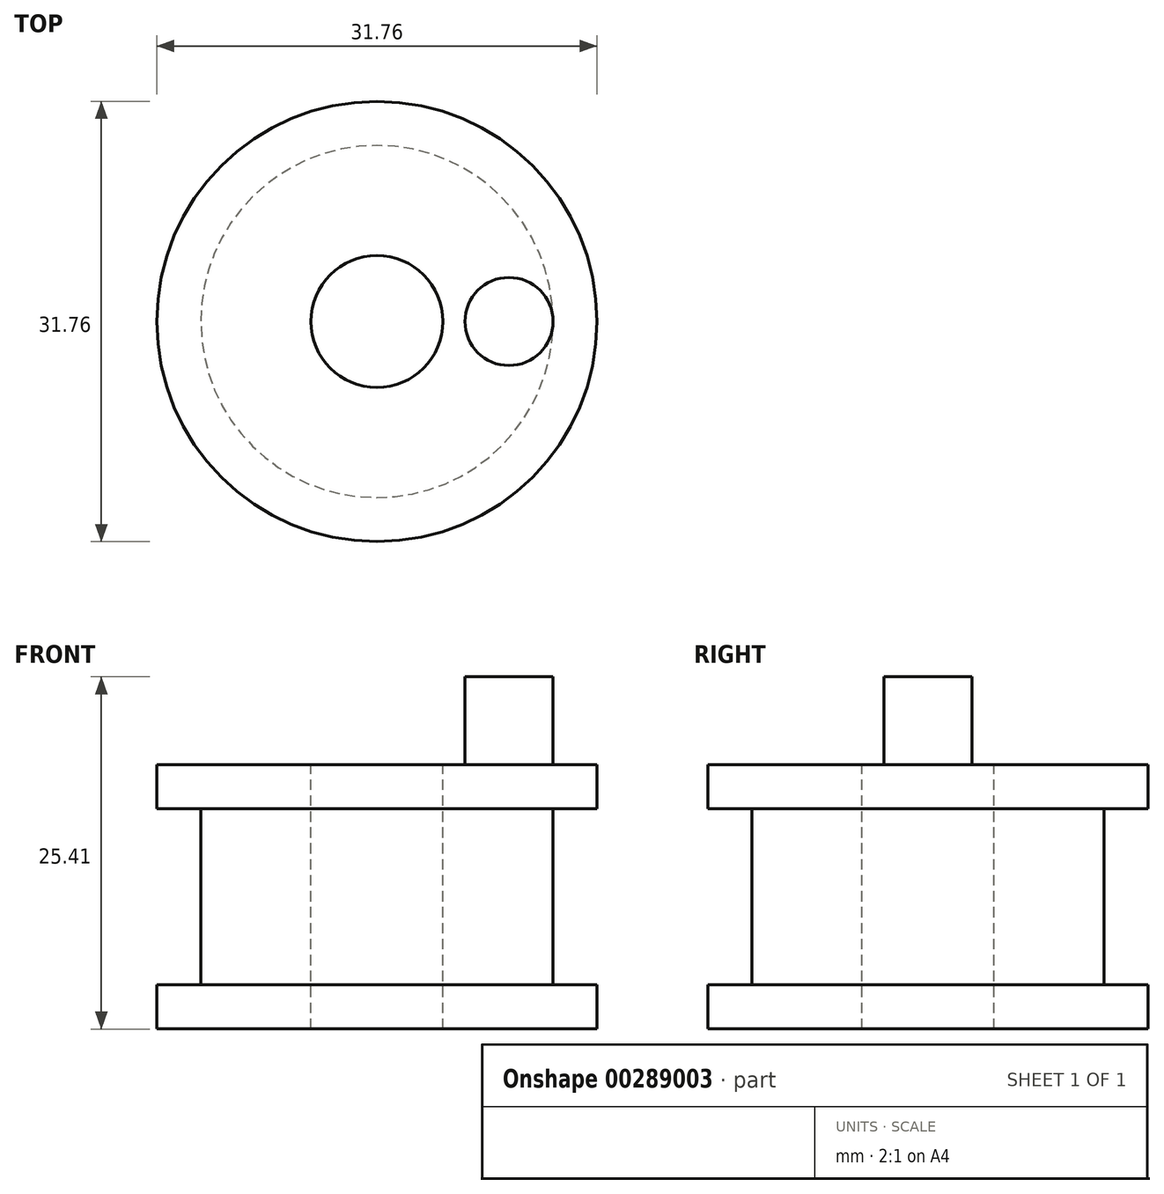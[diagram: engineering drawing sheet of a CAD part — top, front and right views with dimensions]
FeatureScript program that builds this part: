
annotation { "Feature Type Name" : "Feature", "Feature Type Description" : "" }
export const myFeature = defineFeature(function(context is Context, id is Id, definition is map)
    precondition{}
    {
        {
            var Q0;
            Q0=qCreatedBy(makeId("Front.planeOp"),FACE);
            var sketch = newSketch(context, id + "F0", { "sketchPlane" : qUnion([Q0])});
            skLineSegment(sketch, "E0.bottom", {"start": v(-12.7, 6.35) * mm, "end": v(12.7, 6.35) * mm});
            skLineSegment(sketch, "E0.top", {"start": v(-12.7, -6.35) * mm, "end": v(12.7, -6.35) * mm});
            skLineSegment(sketch, "E0.left", {"start": v(-12.7, 6.35) * mm, "end": v(-12.7, -6.35) * mm});
            skLineSegment(sketch, "E0.right", {"start": v(12.7, 6.35) * mm, "end": v(12.7, -6.35) * mm});
            skPoint(sketch, "E0.middle", {"position": v(0, 0) * mm});
            skLineSegment(sketch, "E1", {"start": v(-12.7, 6.35) * mm, "end": v(-15.88, 6.35) * mm});
            skLineSegment(sketch, "E2", {"start": v(-15.88, 6.35) * mm, "end": v(-15.88, 9.53) * mm});
            skLineSegment(sketch, "E3", {"start": v(12.7, 6.35) * mm, "end": v(15.88, 6.35) * mm});
            skLineSegment(sketch, "E4.bottom", {"start": v(-15.88, 6.35) * mm, "end": v(15.88, 6.35) * mm});
            skLineSegment(sketch, "E4.top", {"start": v(-15.88, 9.53) * mm, "end": v(15.88, 9.53) * mm});
            skLineSegment(sketch, "E4.right", {"start": v(15.88, 6.35) * mm, "end": v(15.88, 9.53) * mm});
            skLineSegment(sketch, "E5.MirrorCS", {"start": v(-15.88, -9.53) * mm, "end": v(15.88, -9.53) * mm});
            skLineSegment(sketch, "E6.MirrorCS", {"start": v(-15.88, -6.35) * mm, "end": v(15.88, -6.35) * mm});
            skLineSegment(sketch, "E7.MirrorCS", {"start": v(-15.88, -6.35) * mm, "end": v(-15.88, -9.53) * mm});
            skLineSegment(sketch, "E8.MirrorCS", {"start": v(15.88, -6.35) * mm, "end": v(15.88, -9.53) * mm});
            skPoint(sketch, "E9.orphan", {"position": v(12.7, 0) * mm});
            skPoint(sketch, "E10.start.orphan", {"position": v(-12.7, 0) * mm});
            skLineSegment(sketch, "E11", {"start": v(0, 9.53) * mm, "end": v(0, -9.53) * mm});
            skSolve(sketch);
        }
        {
            var Q0;
            {var subQ0=sQuery(id+"F0.wireOp",EDGE,"E0.left");Q0=makeQuery(id+"F0.imprint","IMPRINT",FACE,{"disambiguationData":[TD([[makeQuery(id+"F0.imprint","IMPRINT",EDGE,{"derivedFrom":subQ0}),1.0]])]});}
            var Q1;
            {var subQ0=sQuery(id+"F0.wireOp",EDGE,"E2");Q1=makeQuery(id+"F0.imprint","IMPRINT",FACE,{"disambiguationData":[TD([[makeQuery(id+"F0.imprint","IMPRINT",EDGE,{"derivedFrom":subQ0}),-1.0]])]});}
            var Q2;
            {var subQ0=sQuery(id+"F0.wireOp",EDGE,"E7.MirrorCS");Q2=makeQuery(id+"F0.imprint","IMPRINT",FACE,{"disambiguationData":[TD([[makeQuery(id+"F0.imprint","IMPRINT",EDGE,{"derivedFrom":subQ0}),1.0]])]});}
            var Q3;
            Q3=sQuery(id+"F0.wireOp",EDGE,"E11");
            revolve(context, id + "F1", {"entities" : qUnion([Q0, Q1, Q2]), "axis" : qUnion([Q3]), "revolveType" : RevolveType.FULL});
        }
        {
            var Q0;
            Q0=makeQuery(id+"F1.opRevolve","SWEPT_FACE",FACE,{"disambiguationData":[OSD([sQuery(id+"F0.wireOp",EDGE,"E4.top")])]});
            var sketch = newSketch(context, id + "F2", { "sketchPlane" : qUnion([Q0])});
            skCircle(sketch, "E12", {"center": v(0, 0) * mm, "radius": 4.76 * mm});
            skCircle(sketch, "E13", {"center": v(9.53, 0) * mm, "radius": 3.18 * mm});
            skSolve(sketch);
        }
        {
            var Q0;
            Q0=sQuery(id+"F2.wireOp",VERTEX,"E12.center");
            var Q1;
            Q1=makeQuery(id+"F1.opRevolve","SWEPT_BODY",BODY,{"disambiguationData":[OSD([sQuery(id+"F0.wireOp",EDGE,"E0.left"),sQuery(id+"F0.wireOp",EDGE,"E4.bottom"),sQuery(id+"F0.wireOp",EDGE,"E4.top"),sQuery(id+"F0.wireOp",EDGE,"E2"),sQuery(id+"F0.wireOp",EDGE,"E5.MirrorCS"),sQuery(id+"F0.wireOp",EDGE,"E6.MirrorCS"),sQuery(id+"F0.wireOp",EDGE,"E7.MirrorCS"),sQuery(id+"F0.wireOp",EDGE,"E11")])]});
            hole(context, id + "F3", {"style" : HoleStyle.SIMPLE, "endStyle" : HoleEndStyle.THROUGH, "holeDiameter" : 9.52 * mm, "tappedDepth" : 12.7 * mm, "tapClearance" : 3, "locations" : qUnion([Q0]), "scope" : qUnion([Q1])});
        }
        {
            var Q0;
            Q0=makeQuery(id+"F2.imprint","IMPRINT",FACE,{"disambiguationData":[TD([[makeQuery(id+"F2.imprint","IMPRINT",EDGE,{"derivedFrom":sQuery(id+"F2.wireOp",EDGE,"E13")}),1.0]])]});
            extrude(context, id + "F4", {"entities" : qUnion([Q0]), "operationType" : NewBodyOperationType.ADD, "depth" : 6.35 * mm});
        }
    });
